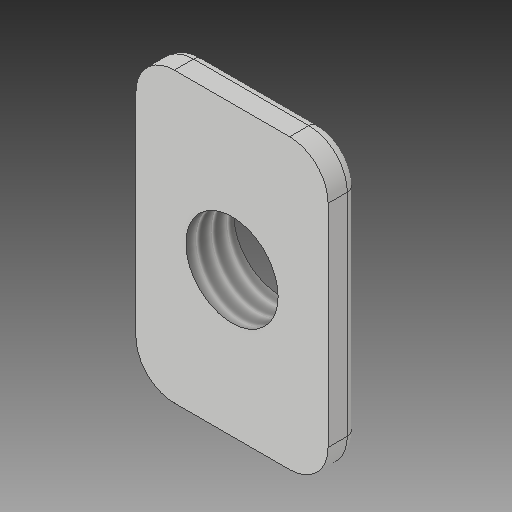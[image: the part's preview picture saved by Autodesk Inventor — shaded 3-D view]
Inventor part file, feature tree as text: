
AUTODESK INVENTOR PART (.ipt)
format: ipt  version: 2018 (Build 220112000, 112)  size: 146,432 bytes
history: native  units: mm
features: other x3, sketch x2
ambient origin geometry x8: Origin, YZ Plane, XZ Plane, XY Plane, X Axis, Y Axis, Z Axis, Center Point
bodies: Solid1 (feature_tree)
feature tree (5):
  other  "M5 Tee Nut_MIR_MIR.ipt"
  other  "Solid1::M5 Tee Nut_MIR_MIR.ipt"
  other  "TaggingFeature1"
  sketch  "Sketch1"  dims[d0=10.0mm]
  sketch  "Sketch2"
